# Revit family: VBGG
name_source: partatom
category: Lighting Fixtures
revit_build: Autodesk Revit Architecture 2012 (Build: 20110309_2315(x64)
units: mm (PartAtom-declared; Revit-internal decimal feet)

## types (1)
- VBGG-VWGG-Wall Mount
    Backbox = Platinum Powder Finish
    Color Filter = 16777215
    Default Elevation = 48.000"
    Description = Wall mount or box/pendent, units completely assembled. Complete with glass globe and guard. Platinum powder finish. 150 or 300 watt sizes.
    Dimming Lamp Color Temperature Shift = <None>
    Family = Outdoor Emergency Lighting
    Glass = Etched Glass
    Lamp = Incandescent.
    Light Source Symbol Size = 3.000"
    Manufacturer = Hubbell Outdoor Lighting
    Manufacturer Fax = (864)-678-1415
    Model = VBGG
    Mounting = Wall Mount
    Product Documentation Link = http://www.hubbelloutdoor.com
    Product Page URL = http://www.hubbelloutdoor.com
    URL = http://www.hubbelloutdoor.com
    Wattage Comments = 150/300 W

## geometry (parser evidence)
native form markers: Sweep x1
no freeform markers — native parametric forms only
